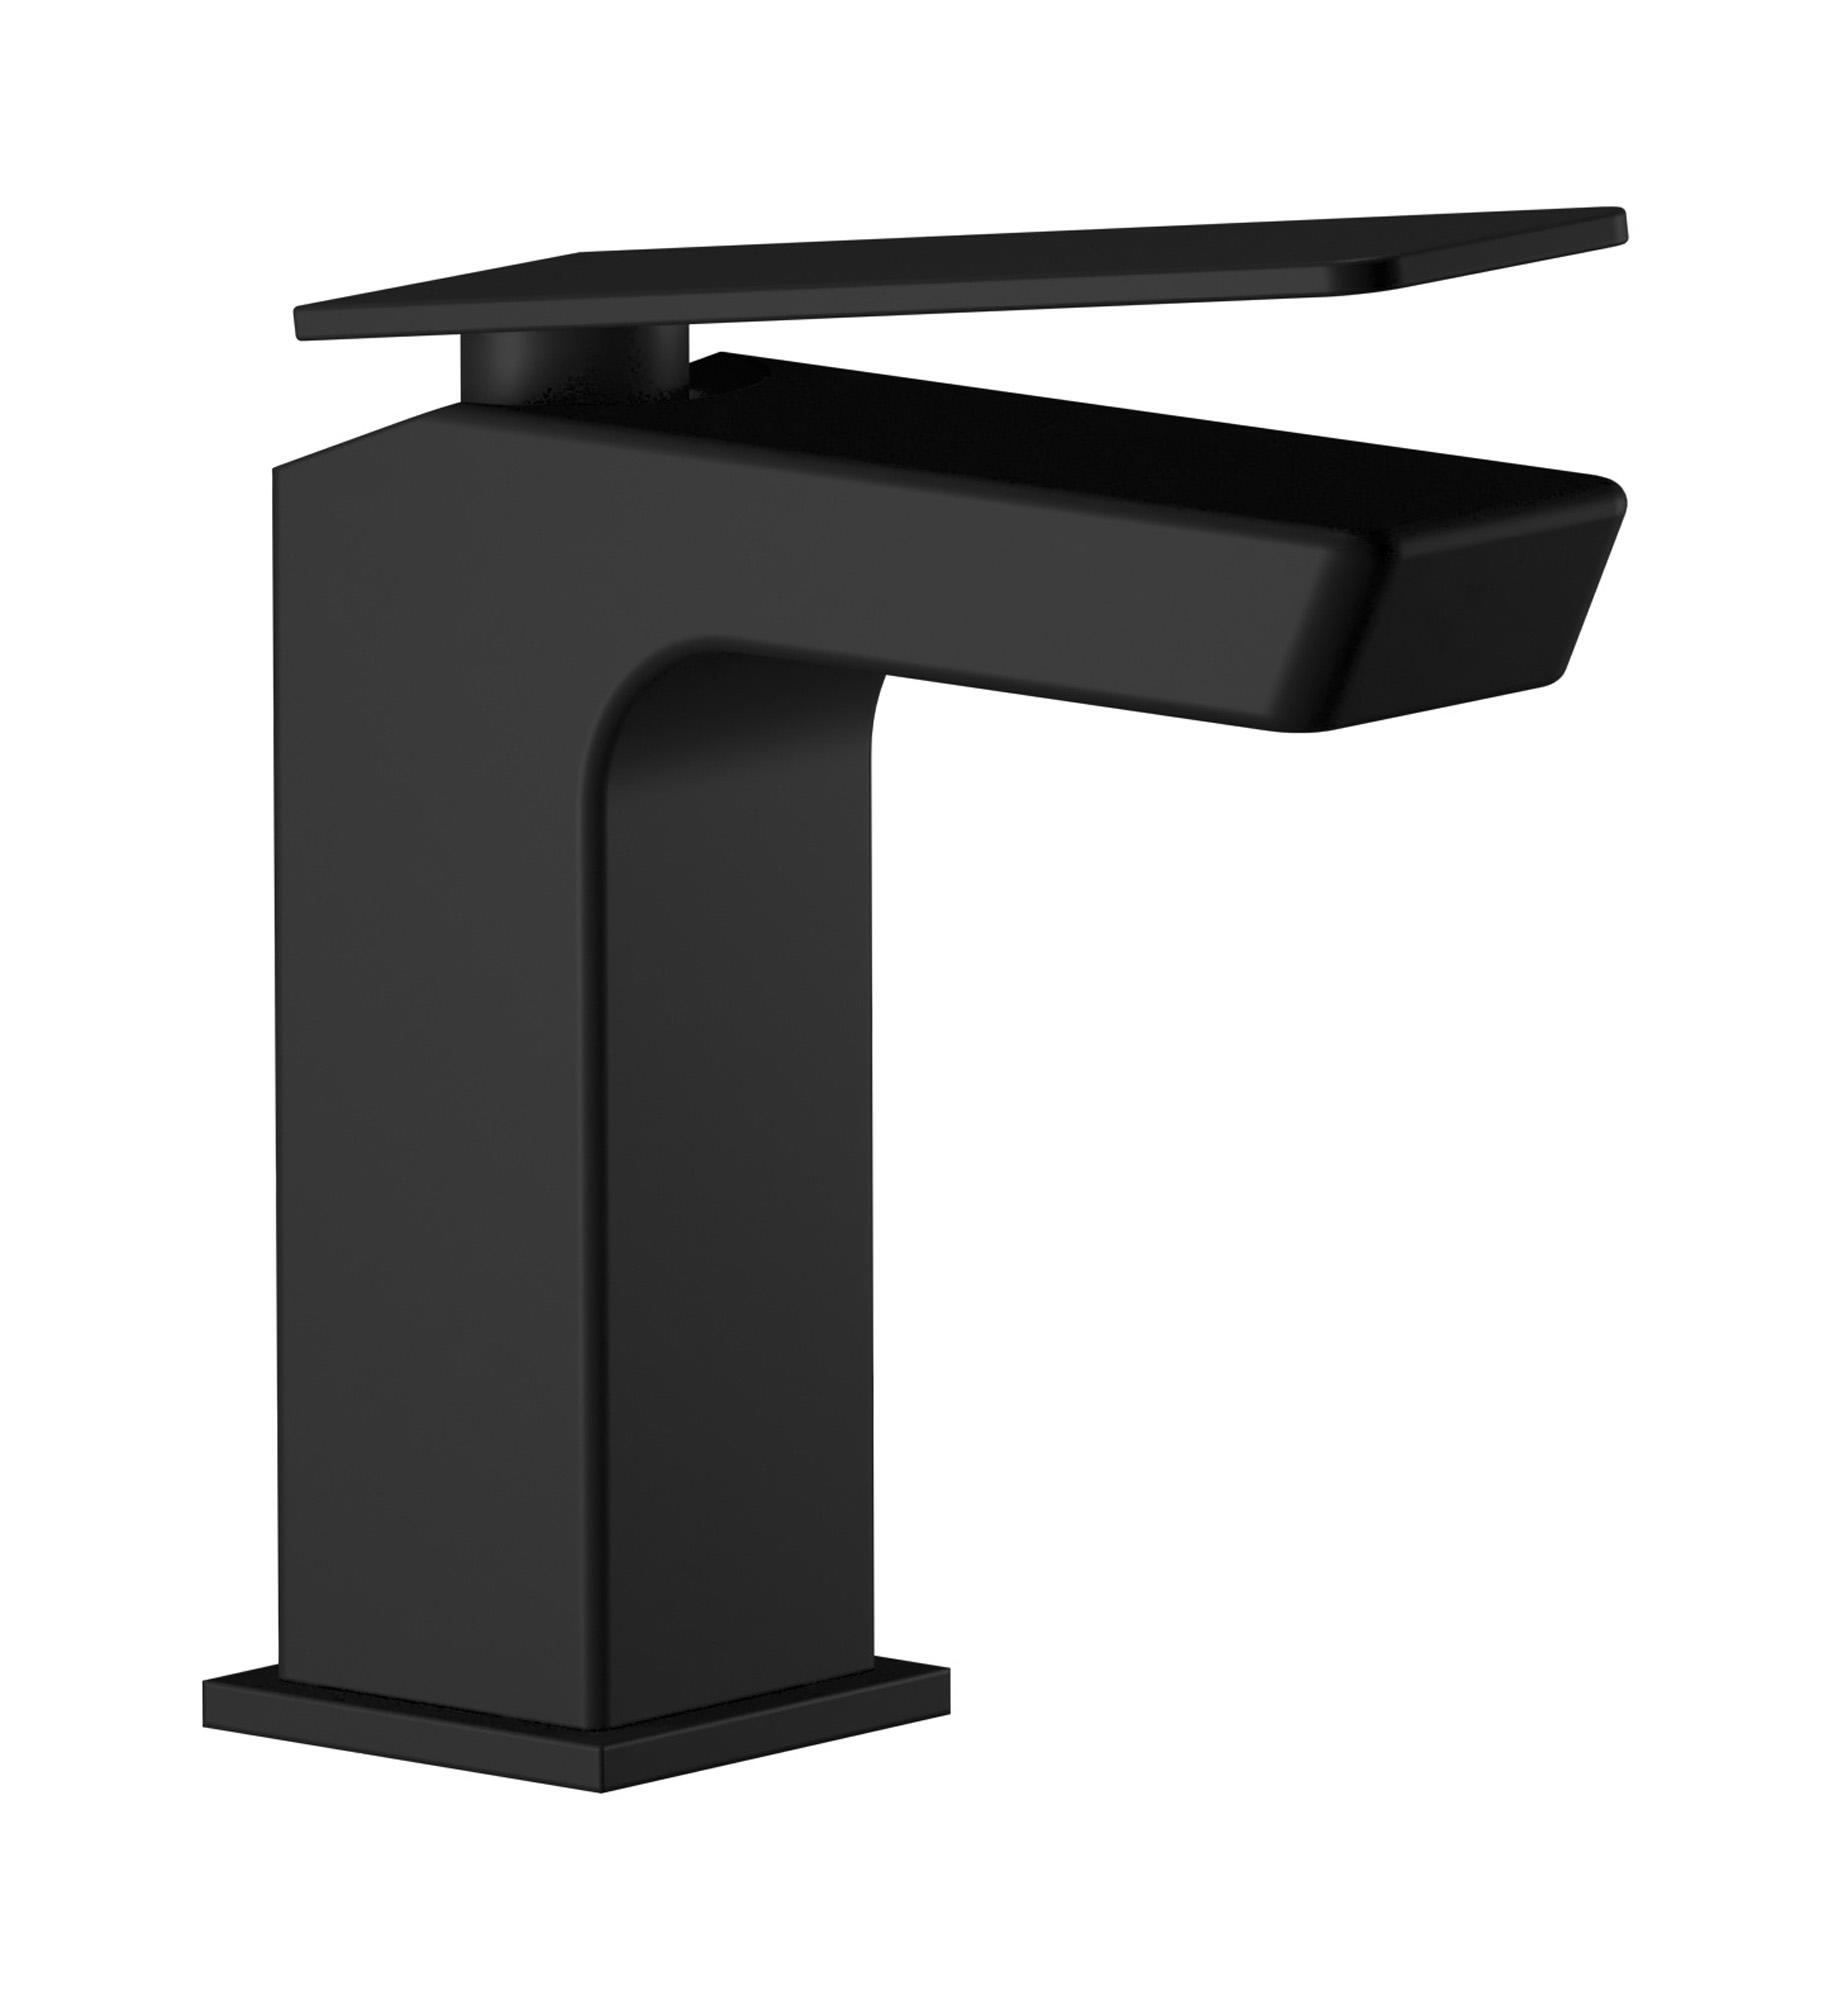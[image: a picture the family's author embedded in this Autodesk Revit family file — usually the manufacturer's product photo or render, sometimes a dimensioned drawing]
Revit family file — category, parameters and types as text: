
# Revit family: K3201
name_source: partatom
category: Apparecchi idraulici
units: mm (PartAtom-declared; Revit-internal decimal feet)

## family parameters
Basato su piano di lavoro = No
Condiviso = No
Mantieni orientamento annotazione = No
Numero OmniClass = 23.45.55.17
Punto di calcolo locali = No
Quota connettore circolare = Usa diametro
Sempre verticale = Sì
Taglio con vuoti quando caricato = No
Tipo di parte = Normale
Titolo OmniClass = Mixing Faucets

## types (8) — shared parameters
Cold water inlet = 10 mm  [stored 0.0328084 ft]
Commenti sul tipo = Washbasin mixer
Connessione CW = No
Connessione HW = No
Connessione di scarico = No
Connessione di ventilazione = No
Descrizione = Mini monohole washbasin mixer complete with drain
Hot water inlet = 10 mm  [stored 0.0328084 ft]
Produttore = IB Rubinetterie S.p.A.
URL = https://www.weareib.it
zero-valued in all types: Prospetto di default

## per-type parameters (varying)
| type | Finishes surface | Immagine tipo | Modello |
| Chrome | IB_Chrome | K3201CC.jpg | K3201CC |
| Brushed nickel | IB_Brushed nickel | K3201SS.jpg | K3201SS |
| Matt white | IB_matt white | K3201BO.jpg | K3201BO |
| Matt black | IB_matt black | K3201NP.jpg | K3201NP |
| Pale gold | IB_Pale gold | K3201II.jpg | K3201II |
| Brushed pale gold | IB_brushed pale gold | K3201IS.jpg | K3201IS |
| Rose gold | IB_Rose gold | K3201RS.jpg | K3201RS |
| Gold | IB_gold | K3201OO.jpg | K3201OO |

note: [stored X ft] marks values corroborated as IEEE doubles in the binary element streams (Revit-internal decimal feet)
